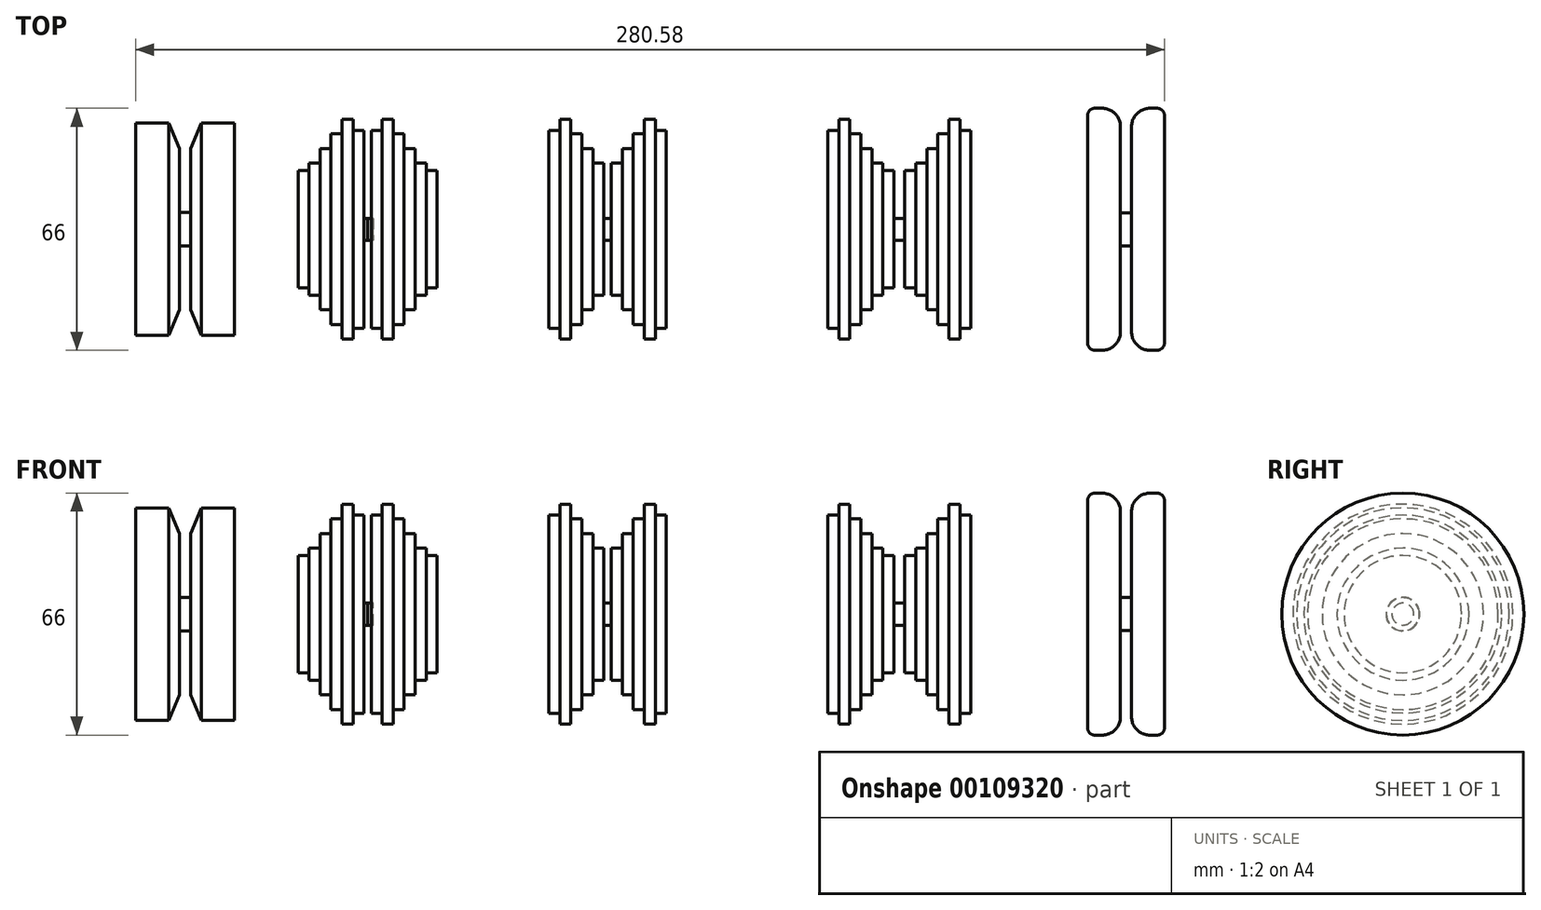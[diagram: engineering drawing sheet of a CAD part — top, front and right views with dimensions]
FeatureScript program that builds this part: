
annotation { "Feature Type Name" : "Feature", "Feature Type Description" : "" }
export const myFeature = defineFeature(function(context is Context, id is Id, definition is map)
    precondition{}
    {
        {
            var Q0;
            Q0=qCreatedBy(makeId("Right.planeOp"),FACE);
            var sketch = newSketch(context, id + "F0", { "sketchPlane" : qUnion([Q0])});
            skCircle(sketch, "E0", {"center": v(0, 0) * mm, "radius": 3 * mm});
            skSolve(sketch);
        }
        {
            var Q0;
            Q0 = qSketchRegion(id + "F0", true);
            extrude(context, id + "F1", {"entities" : qUnion([Q0]), "depth" : 1.5 * mm});
        }
        {
            var Q0;
            Q0=qCreatedBy(makeId("Front.planeOp"),FACE);
            var sketch = newSketch(context, id + "F2", { "sketchPlane" : qUnion([Q0])});
            skLineSegment(sketch, "E1", {"start": v(-0.02, 3) * mm, "end": v(1.48, 3) * mm});
            skLineSegment(sketch, "E2", {"start": v(1.48, 3) * mm, "end": v(0.98, 3) * mm});
            skLineSegment(sketch, "E3", {"start": v(0.98, 3) * mm, "end": v(0.98, 27) * mm});
            skLineSegment(sketch, "E4", {"start": v(0.98, 27) * mm, "end": v(3.98, 27) * mm});
            skLineSegment(sketch, "E5", {"start": v(3.98, 27) * mm, "end": v(3.98, 30) * mm});
            skLineSegment(sketch, "E6", {"start": v(3.98, 30) * mm, "end": v(6.98, 30) * mm});
            skLineSegment(sketch, "E7", {"start": v(6.98, 30) * mm, "end": v(6.98, 26) * mm});
            skLineSegment(sketch, "E8", {"start": v(6.98, 26) * mm, "end": v(9.98, 26) * mm});
            skLineSegment(sketch, "E9", {"start": v(9.98, 26) * mm, "end": v(9.98, 22) * mm});
            skLineSegment(sketch, "E10", {"start": v(9.98, 22) * mm, "end": v(12.98, 22) * mm});
            skLineSegment(sketch, "E11", {"start": v(15.98, 0) * mm, "end": v(0, 0) * mm});
            skLineSegment(sketch, "E12", {"start": v(12.98, 22) * mm, "end": v(12.98, 18) * mm});
            skLineSegment(sketch, "E13", {"start": v(12.98, 18) * mm, "end": v(15.98, 18) * mm});
            skLineSegment(sketch, "E14", {"start": v(-15.99, 0) * mm, "end": v(96.16, 0) * mm});
            skLineSegment(sketch, "E15", {"start": v(-0.02, 3) * mm, "end": v(0, 0) * mm});
            skLineSegment(sketch, "E16", {"start": v(41.2, 32.66) * mm, "end": v(41.2, -11.03) * mm});
            skLineSegment(sketch, "E17.MirrorCS", {"start": v(81.44, 3) * mm, "end": v(81.44, 27) * mm});
            skLineSegment(sketch, "E18.MirrorCS", {"start": v(75.44, 30) * mm, "end": v(75.44, 26) * mm});
            skLineSegment(sketch, "E19.MirrorCS", {"start": v(78.44, 30) * mm, "end": v(75.44, 30) * mm});
            skLineSegment(sketch, "E20.MirrorCS", {"start": v(75.44, 26) * mm, "end": v(72.44, 26) * mm});
            skLineSegment(sketch, "E21.MirrorCS", {"start": v(72.44, 26) * mm, "end": v(72.44, 22) * mm});
            skLineSegment(sketch, "E22.MirrorCS", {"start": v(72.44, 22) * mm, "end": v(69.44, 22) * mm});
            skLineSegment(sketch, "E23.MirrorCS", {"start": v(69.44, 22) * mm, "end": v(69.44, 18) * mm});
            skLineSegment(sketch, "E24.MirrorCS", {"start": v(69.44, 18) * mm, "end": v(66.44, 18) * mm});
            skLineSegment(sketch, "E25.MirrorCS", {"start": v(78.44, 27) * mm, "end": v(78.44, 30) * mm});
            skLineSegment(sketch, "E26.MirrorCS", {"start": v(66.44, 18) * mm, "end": v(66.44, 0) * mm});
            skLineSegment(sketch, "E27.MirrorCS", {"start": v(81.44, 27) * mm, "end": v(78.44, 27) * mm});
            skLineSegment(sketch, "E28", {"start": v(81.44, 3) * mm, "end": v(81.44, 0) * mm});
            skLineSegment(sketch, "E29", {"start": v(81.44, 0) * mm, "end": v(65.44, 0) * mm});
            skLineSegment(sketch, "E30", {"start": v(65.44, 0) * mm, "end": v(65.44, 3) * mm});
            skLineSegment(sketch, "E31", {"start": v(65.44, 3) * mm, "end": v(66.94, 3) * mm});
            skLineSegment(sketch, "E32", {"start": v(66.94, 3) * mm, "end": v(66.44, 3) * mm});
            skLineSegment(sketch, "E33.MirrorCS", {"start": v(63.94, 3) * mm, "end": v(64.44, 3) * mm});
            skLineSegment(sketch, "E34.MirrorCS", {"start": v(65.44, 3) * mm, "end": v(63.94, 3) * mm});
            skLineSegment(sketch, "E35.MirrorCS", {"start": v(61.44, 18) * mm, "end": v(64.44, 18) * mm});
            skLineSegment(sketch, "E36.MirrorCS", {"start": v(49.44, 3) * mm, "end": v(49.44, 0) * mm});
            skLineSegment(sketch, "E37.MirrorCS", {"start": v(58.44, 26) * mm, "end": v(58.44, 22) * mm});
            skLineSegment(sketch, "E38.MirrorCS", {"start": v(64.44, 18) * mm, "end": v(64.44, 0) * mm});
            skLineSegment(sketch, "E39.MirrorCS", {"start": v(61.44, 22) * mm, "end": v(61.44, 18) * mm});
            skLineSegment(sketch, "E40.MirrorCS", {"start": v(49.44, 3) * mm, "end": v(49.44, 27) * mm});
            skLineSegment(sketch, "E41.MirrorCS", {"start": v(52.44, 27) * mm, "end": v(52.44, 30) * mm});
            skLineSegment(sketch, "E42.MirrorCS", {"start": v(58.44, 22) * mm, "end": v(61.44, 22) * mm});
            skLineSegment(sketch, "E43.MirrorCS", {"start": v(49.44, 0) * mm, "end": v(65.44, 0) * mm});
            skLineSegment(sketch, "E44.MirrorCS", {"start": v(52.44, 30) * mm, "end": v(55.44, 30) * mm});
            skLineSegment(sketch, "E45.MirrorCS", {"start": v(55.44, 30) * mm, "end": v(55.44, 26) * mm});
            skLineSegment(sketch, "E46.MirrorCS", {"start": v(49.44, 27) * mm, "end": v(52.44, 27) * mm});
            skLineSegment(sketch, "E47.MirrorCS", {"start": v(55.44, 26) * mm, "end": v(58.44, 26) * mm});
            skLineSegment(sketch, "E48", {"start": v(15.98, 0) * mm, "end": v(18.98, 0) * mm});
            skLineSegment(sketch, "E49", {"start": v(15.98, 18) * mm, "end": v(15.98, 16) * mm});
            skLineSegment(sketch, "E50", {"start": v(15.98, 16) * mm, "end": v(18.98, 16) * mm});
            skLineSegment(sketch, "E51", {"start": v(18.98, 16) * mm, "end": v(18.98, 0) * mm});
            skLineSegment(sketch, "E52.MirrorCS", {"start": v(-15.98, 0) * mm, "end": v(-18.98, 0) * mm});
            skLineSegment(sketch, "E53.MirrorCS", {"start": v(0.02, 3) * mm, "end": v(0, 0) * mm});
            skLineSegment(sketch, "E54.MirrorCS", {"start": v(-12.98, 18) * mm, "end": v(-15.98, 18) * mm});
            skLineSegment(sketch, "E55.MirrorCS", {"start": v(-3.98, 27) * mm, "end": v(-3.98, 30) * mm});
            skLineSegment(sketch, "E56.MirrorCS", {"start": v(-3.98, 30) * mm, "end": v(-6.98, 30) * mm});
            skLineSegment(sketch, "E57.MirrorCS", {"start": v(-15.98, 16) * mm, "end": v(-18.98, 16) * mm});
            skLineSegment(sketch, "E58.MirrorCS", {"start": v(-6.98, 26) * mm, "end": v(-9.98, 26) * mm});
            skLineSegment(sketch, "E59.MirrorCS", {"start": v(-0.98, 27) * mm, "end": v(-3.98, 27) * mm});
            skLineSegment(sketch, "E60.MirrorCS", {"start": v(-9.98, 22) * mm, "end": v(-12.98, 22) * mm});
            skLineSegment(sketch, "E61.MirrorCS", {"start": v(0.02, 3) * mm, "end": v(-1.48, 3) * mm});
            skLineSegment(sketch, "E62.MirrorCS", {"start": v(-1.48, 3) * mm, "end": v(-0.98, 3) * mm});
            skLineSegment(sketch, "E63.MirrorCS", {"start": v(-18.98, 16) * mm, "end": v(-18.98, 0) * mm});
            skLineSegment(sketch, "E64.MirrorCS", {"start": v(-12.98, 22) * mm, "end": v(-12.98, 18) * mm});
            skLineSegment(sketch, "E65.MirrorCS", {"start": v(-6.98, 30) * mm, "end": v(-6.98, 26) * mm});
            skLineSegment(sketch, "E66.MirrorCS", {"start": v(-15.98, 18) * mm, "end": v(-15.98, 16) * mm});
            skLineSegment(sketch, "E67.MirrorCS", {"start": v(-0.98, 3) * mm, "end": v(-0.98, 27) * mm});
            skLineSegment(sketch, "E68.MirrorCS", {"start": v(-9.98, 26) * mm, "end": v(-9.98, 22) * mm});
            skLineSegment(sketch, "E69.MirrorCS", {"start": v(-15.98, 0) * mm, "end": v(0, 0) * mm});
            skLineSegment(sketch, "E70", {"start": v(82.73, 41.31) * mm, "end": v(82.73, -26) * mm});
            skLineSegment(sketch, "E71.MirrorCS", {"start": v(164.49, 27) * mm, "end": v(161.49, 27) * mm});
            skLineSegment(sketch, "E72.MirrorCS", {"start": v(161.49, 27) * mm, "end": v(161.49, 30) * mm});
            skLineSegment(sketch, "E73.MirrorCS", {"start": v(155.49, 22) * mm, "end": v(152.49, 22) * mm});
            skLineSegment(sketch, "E74.MirrorCS", {"start": v(149.49, 16) * mm, "end": v(146.49, 16) * mm});
            skLineSegment(sketch, "E75.MirrorCS", {"start": v(152.49, 22) * mm, "end": v(152.49, 18) * mm});
            skLineSegment(sketch, "E76.MirrorCS", {"start": v(149.49, 18) * mm, "end": v(149.49, 16) * mm});
            skLineSegment(sketch, "E77.MirrorCS", {"start": v(155.49, 26) * mm, "end": v(155.49, 22) * mm});
            skLineSegment(sketch, "E78.MirrorCS", {"start": v(161.49, 30) * mm, "end": v(158.49, 30) * mm});
            skLineSegment(sketch, "E79.MirrorCS", {"start": v(152.49, 18) * mm, "end": v(149.49, 18) * mm});
            skLineSegment(sketch, "E80.MirrorCS", {"start": v(158.49, 26) * mm, "end": v(155.49, 26) * mm});
            skLineSegment(sketch, "E81.MirrorCS", {"start": v(158.49, 30) * mm, "end": v(158.49, 26) * mm});
            skLineSegment(sketch, "E82.MirrorCS", {"start": v(164.49, 3) * mm, "end": v(164.49, 27) * mm});
            skLineSegment(sketch, "E83.MirrorCS", {"start": v(146.49, 16) * mm, "end": v(146.49, 0) * mm});
            skLineSegment(sketch, "E84", {"start": v(164.49, 3) * mm, "end": v(164.49, 0) * mm});
            skLineSegment(sketch, "E85", {"start": v(164.49, 0) * mm, "end": v(146.49, 0) * mm});
            skLineSegment(sketch, "E86", {"start": v(146.49, 0) * mm, "end": v(144.99, 0) * mm});
            skLineSegment(sketch, "E87", {"start": v(144.99, 0) * mm, "end": v(144.99, 3) * mm});
            skLineSegment(sketch, "E88", {"start": v(144.99, 3) * mm, "end": v(146.49, 3) * mm});
            skLineSegment(sketch, "E89.MirrorCS", {"start": v(143.49, 0) * mm, "end": v(144.99, 0) * mm});
            skLineSegment(sketch, "E90.MirrorCS", {"start": v(144.99, 3) * mm, "end": v(143.49, 3) * mm});
            skLineSegment(sketch, "E91.MirrorCS", {"start": v(131.49, 26) * mm, "end": v(134.49, 26) * mm});
            skLineSegment(sketch, "E92.MirrorCS", {"start": v(143.49, 16) * mm, "end": v(143.49, 0) * mm});
            skLineSegment(sketch, "E93.MirrorCS", {"start": v(140.49, 18) * mm, "end": v(140.49, 16) * mm});
            skLineSegment(sketch, "E94.MirrorCS", {"start": v(125.49, 3) * mm, "end": v(125.49, 0) * mm});
            skLineSegment(sketch, "E95.MirrorCS", {"start": v(134.49, 22) * mm, "end": v(137.49, 22) * mm});
            skLineSegment(sketch, "E96.MirrorCS", {"start": v(128.49, 30) * mm, "end": v(131.49, 30) * mm});
            skLineSegment(sketch, "E97.MirrorCS", {"start": v(125.49, 0) * mm, "end": v(143.49, 0) * mm});
            skLineSegment(sketch, "E98.MirrorCS", {"start": v(140.49, 16) * mm, "end": v(143.49, 16) * mm});
            skLineSegment(sketch, "E99.MirrorCS", {"start": v(125.49, 27) * mm, "end": v(128.49, 27) * mm});
            skLineSegment(sketch, "E100.MirrorCS", {"start": v(137.49, 18) * mm, "end": v(140.49, 18) * mm});
            skLineSegment(sketch, "E101.MirrorCS", {"start": v(125.49, 3) * mm, "end": v(125.49, 27) * mm});
            skLineSegment(sketch, "E102.MirrorCS", {"start": v(137.49, 22) * mm, "end": v(137.49, 18) * mm});
            skLineSegment(sketch, "E103.MirrorCS", {"start": v(131.49, 30) * mm, "end": v(131.49, 26) * mm});
            skLineSegment(sketch, "E104.MirrorCS", {"start": v(134.49, 26) * mm, "end": v(134.49, 22) * mm});
            skLineSegment(sketch, "E105.MirrorCS", {"start": v(128.49, 27) * mm, "end": v(128.49, 30) * mm});
            skSolve(sketch);
        }
        {
            var Q0;
            {var subQ0=sQuery(id+"F2.wireOp",EDGE,"E86");var subQ6=makeQuery(id+"F2.imprint","IMPRINT",EDGE,{"derivedFrom":sQuery(id+"F2.wireOp",EDGE,"E87")});var subQ28=sQuery(id+"F2.wireOp",EDGE,"E35.MirrorCS");var subQ30=sQuery(id+"F2.wireOp",EDGE,"E30");var subQ32=makeQuery(id+"F2.imprint","IMPRINT",EDGE,{"derivedFrom":subQ30});var subQ34=sQuery(id+"F2.wireOp",EDGE,"E15");var subQ38=makeQuery(id+"F2.imprint","IMPRINT",EDGE,{"derivedFrom":subQ34});var subQ46=sQuery(id+"F2.wireOp",EDGE,"E3");Q0=qUnion([makeQuery(id+"F2.imprint","IMPRINT",FACE,{"disambiguationData":[TD([[subQ38,1.0]])]}),makeQuery(id+"F2.imprint","IMPRINT",FACE,{"disambiguationData":[TD([[makeQuery(id+"F2.imprint","IMPRINT",EDGE,{"derivedFrom":subQ46}),-1.0]])]}),makeQuery(id+"F2.imprint","IMPRINT",FACE,{"disambiguationData":[TD([[subQ38,-1.0]])]}),makeQuery(id+"F2.imprint","IMPRINT",FACE,{"disambiguationData":[TD([[subQ32,-1.0]])]}),makeQuery(id+"F2.imprint","IMPRINT",FACE,{"disambiguationData":[TD([[subQ32,1.0]])]}),makeQuery(id+"F2.imprint","IMPRINT",FACE,{"disambiguationData":[TD([[makeQuery(id+"F2.imprint","IMPRINT",EDGE,{"derivedFrom":subQ28}),-1.0]])]}),makeQuery(id+"F2.imprint","IMPRINT",FACE,{"disambiguationData":[TD([[makeQuery(id+"F2.imprint","IMPRINT",EDGE,{"derivedFrom":sQuery(id+"F2.wireOp",EDGE,"E17.MirrorCS")}),1.0]])]}),makeQuery(id+"F2.imprint","IMPRINT",FACE,{"disambiguationData":[TD([[subQ6,1.0]])]}),makeQuery(id+"F2.imprint","IMPRINT",FACE,{"disambiguationData":[TD([[makeQuery(id+"F2.imprint","IMPRINT",EDGE,{"derivedFrom":sQuery(id+"F2.wireOp",EDGE,"E71.MirrorCS")}),1.0]])]}),makeQuery(id+"F2.imprint","IMPRINT",FACE,{"disambiguationData":[TD([[makeQuery(id+"F2.imprint","IMPRINT",EDGE,{"derivedFrom":sQuery(id+"F2.wireOp",EDGE,"E91.MirrorCS")}),-1.0]])]}),makeQuery(id+"F2.imprint","IMPRINT",FACE,{"disambiguationData":[TD([[makeQuery(id+"F2.imprint","IMPRINT",EDGE,{"derivedFrom":subQ0}),-1.0]])]})]);}
            var Q1;
            Q1=sQuery(id+"F2.wireOp",EDGE,"E11");
            revolve(context, id + "F3", {"entities" : qUnion([Q0]), "axis" : qUnion([Q1]), "revolveType" : RevolveType.FULL});
        }
        {
            var Q0;
            Q0=qCreatedBy(makeId("Front.planeOp"),FACE);
            var sketch = newSketch(context, id + "F4", { "sketchPlane" : qUnion([Q0])});
            skLineSegment(sketch, "E106", {"start": v(-49.78, 0) * mm, "end": v(-49.78, 4.6) * mm});
            skLineSegment(sketch, "E107", {"start": v(-49.78, 4.6) * mm, "end": v(-48.28, 4.6) * mm});
            skLineSegment(sketch, "E108", {"start": v(-48.28, 4.6) * mm, "end": v(-48.28, 15.62) * mm});
            skLineSegment(sketch, "E109", {"start": v(-42.28, 29) * mm, "end": v(-40.88, 29) * mm});
            skLineSegment(sketch, "E110", {"start": v(-42.28, 29) * mm, "end": v(-42.28, 29) * mm});
            skLineSegment(sketch, "E111", {"start": v(-42.28, 29) * mm, "end": v(-39.28, 29) * mm});
            skLineSegment(sketch, "E112", {"start": v(-39.28, 29) * mm, "end": v(-36.28, 29) * mm});
            skLineSegment(sketch, "E113", {"start": v(-36.28, 29) * mm, "end": v(-36.28, 0) * mm});
            skLineSegment(sketch, "E114", {"start": v(-36.28, 0) * mm, "end": v(-49.78, 0) * mm});
            skPoint(sketch, "E115.visualSharp", {"position": v(-45.28, 29) * mm});
            skPoint(sketch, "E116.orphan", {"position": v(-48.28, 22) * mm});
            skLineSegment(sketch, "E117.MirrorCS", {"start": v(-57.28, 29) * mm, "end": v(-58.68, 29) * mm});
            skLineSegment(sketch, "E118.MirrorCS", {"start": v(-49.78, 4.6) * mm, "end": v(-51.28, 4.6) * mm});
            skLineSegment(sketch, "E119.MirrorCS", {"start": v(-57.28, 29) * mm, "end": v(-60.28, 29) * mm});
            skLineSegment(sketch, "E120.MirrorCS", {"start": v(-63.28, 0) * mm, "end": v(-49.78, 0) * mm});
            skPoint(sketch, "E121.MirrorP", {"position": v(-51.28, 22) * mm});
            skPoint(sketch, "E122.MirrorP", {"position": v(-54.28, 29) * mm});
            skLineSegment(sketch, "E123.MirrorCS", {"start": v(-51.28, 4.6) * mm, "end": v(-51.28, 15.62) * mm});
            skLineSegment(sketch, "E124.MirrorCS", {"start": v(-60.28, 29) * mm, "end": v(-63.28, 29) * mm});
            skLineSegment(sketch, "E125.MirrorCS", {"start": v(-63.28, 29) * mm, "end": v(-63.28, 0) * mm});
            skLineSegment(sketch, "E126", {"start": v(-42.28, 29) * mm, "end": v(-45.28, 29) * mm});
            skLineSegment(sketch, "E127", {"start": v(-48.28, 15.62) * mm, "end": v(-48.28, 22) * mm});
            skLineSegment(sketch, "E128", {"start": v(-45.28, 29) * mm, "end": v(-48.28, 22) * mm});
            skLineSegment(sketch, "E129", {"start": v(-57.28, 29) * mm, "end": v(-54.28, 29) * mm});
            skLineSegment(sketch, "E130", {"start": v(-54.28, 29) * mm, "end": v(-51.28, 22) * mm});
            skLineSegment(sketch, "E131", {"start": v(-51.28, 22) * mm, "end": v(-51.28, 15.62) * mm});
            skSolve(sketch);
        }
        {
            var Q0;
            Q0=makeQuery(id+"F4.imprint","IMPRINT",FACE,{"disambiguationData":[TD([[makeQuery(id+"F4.imprint","IMPRINT",EDGE,{"derivedFrom":sQuery(id+"F4.wireOp",EDGE,"E106")}),-1.0]])]});
            var Q1;
            Q1=makeQuery(id+"F4.imprint","IMPRINT",FACE,{"disambiguationData":[TD([[makeQuery(id+"F4.imprint","IMPRINT",EDGE,{"derivedFrom":sQuery(id+"F4.wireOp",EDGE,"E106")}),1.0]])]});
            var Q2;
            Q2=sQuery(id+"F4.wireOp",EDGE,"E114");
            revolve(context, id + "F5", {"entities" : qUnion([Q0, Q1]), "axis" : qUnion([Q2]), "revolveType" : RevolveType.FULL});
        }
        {
            var Q0;
            Q0=qCreatedBy(makeId("Front.planeOp"),FACE);
            var sketch = newSketch(context, id + "F6", { "sketchPlane" : qUnion([Q0])});
            skLineSegment(sketch, "E132", {"start": v(208.3, 0) * mm, "end": v(217.3, 0) * mm});
            skLineSegment(sketch, "E133", {"start": v(217.3, 0) * mm, "end": v(217.3, 31) * mm});
            skLineSegment(sketch, "E134", {"start": v(215.3, 33) * mm, "end": v(213.3, 33) * mm});
            skLineSegment(sketch, "E135", {"start": v(208.3, 28) * mm, "end": v(208.3, 0) * mm});
            skLineSegment(sketch, "E136", {"start": v(205.3, 0) * mm, "end": v(208.3, 0) * mm});
            skLineSegment(sketch, "E137", {"start": v(208.3, 0) * mm, "end": v(208.3, 4.5) * mm});
            skLineSegment(sketch, "E138", {"start": v(208.3, 4.5) * mm, "end": v(205.3, 4.5) * mm});
            skLineSegment(sketch, "E139", {"start": v(205.3, 4.5) * mm, "end": v(205.3, 0) * mm});
            skLineSegment(sketch, "E140", {"start": v(196.3, 0) * mm, "end": v(205.3, 0) * mm});
            skLineSegment(sketch, "E141", {"start": v(205.3, 0) * mm, "end": v(205.3, 28) * mm});
            skLineSegment(sketch, "E142", {"start": v(200.3, 33) * mm, "end": v(198.3, 33) * mm});
            skLineSegment(sketch, "E143", {"start": v(196.3, 31) * mm, "end": v(196.3, 0) * mm});
            skPoint(sketch, "E144.visualSharp", {"position": v(196.3, 33) * mm});
            skArc(sketch, "E144.filletArc", {"start": v(198.3, 33) * mm, "mid": v(196.89, 32.41) * mm, "end": v(196.3, 31) * mm});
            skPoint(sketch, "E145.visualSharp", {"position": v(217.3, 33) * mm});
            skArc(sketch, "E145.filletArc", {"start": v(217.3, 31) * mm, "mid": v(216.72, 32.41) * mm, "end": v(215.3, 33) * mm});
            skPoint(sketch, "E146.visualSharp", {"position": v(205.3, 33) * mm});
            skArc(sketch, "E146.filletArc", {"start": v(205.3, 28) * mm, "mid": v(203.84, 31.54) * mm, "end": v(200.3, 33) * mm});
            skPoint(sketch, "E147.visualSharp", {"position": v(208.3, 33) * mm});
            skArc(sketch, "E147.filletArc", {"start": v(213.3, 33) * mm, "mid": v(209.77, 31.54) * mm, "end": v(208.3, 28) * mm});
            skSolve(sketch);
        }
        {
            var Q0;
            Q0=makeQuery(id+"F6.imprint","IMPRINT",FACE,{"disambiguationData":[TD([[makeQuery(id+"F6.imprint","IMPRINT",EDGE,{"derivedFrom":sQuery(id+"F6.wireOp",EDGE,"E139")}),-1.0]])]});
            var Q1;
            {var subQ0=sQuery(id+"F6.wireOp",EDGE,"E136");Q1=makeQuery(id+"F6.imprint","IMPRINT",FACE,{"disambiguationData":[TD([[makeQuery(id+"F6.imprint","IMPRINT",EDGE,{"derivedFrom":subQ0}),1.0]])]});}
            var Q2;
            {var subQ3=sQuery(id+"F6.wireOp",EDGE,"E132");Q2=makeQuery(id+"F6.imprint","IMPRINT",FACE,{"disambiguationData":[TD([[makeQuery(id+"F6.imprint","IMPRINT",EDGE,{"derivedFrom":subQ3}),1.0]])]});}
            var Q3;
            Q3=sQuery(id+"F6.wireOp",EDGE,"E136");
            revolve(context, id + "F7", {"surfaceOperationType" : NewSurfaceOperationType.NEW, "entities" : qUnion([Q0, Q1, Q2]), "axis" : qUnion([Q3]), "revolveType" : RevolveType.FULL});
        }
    });
